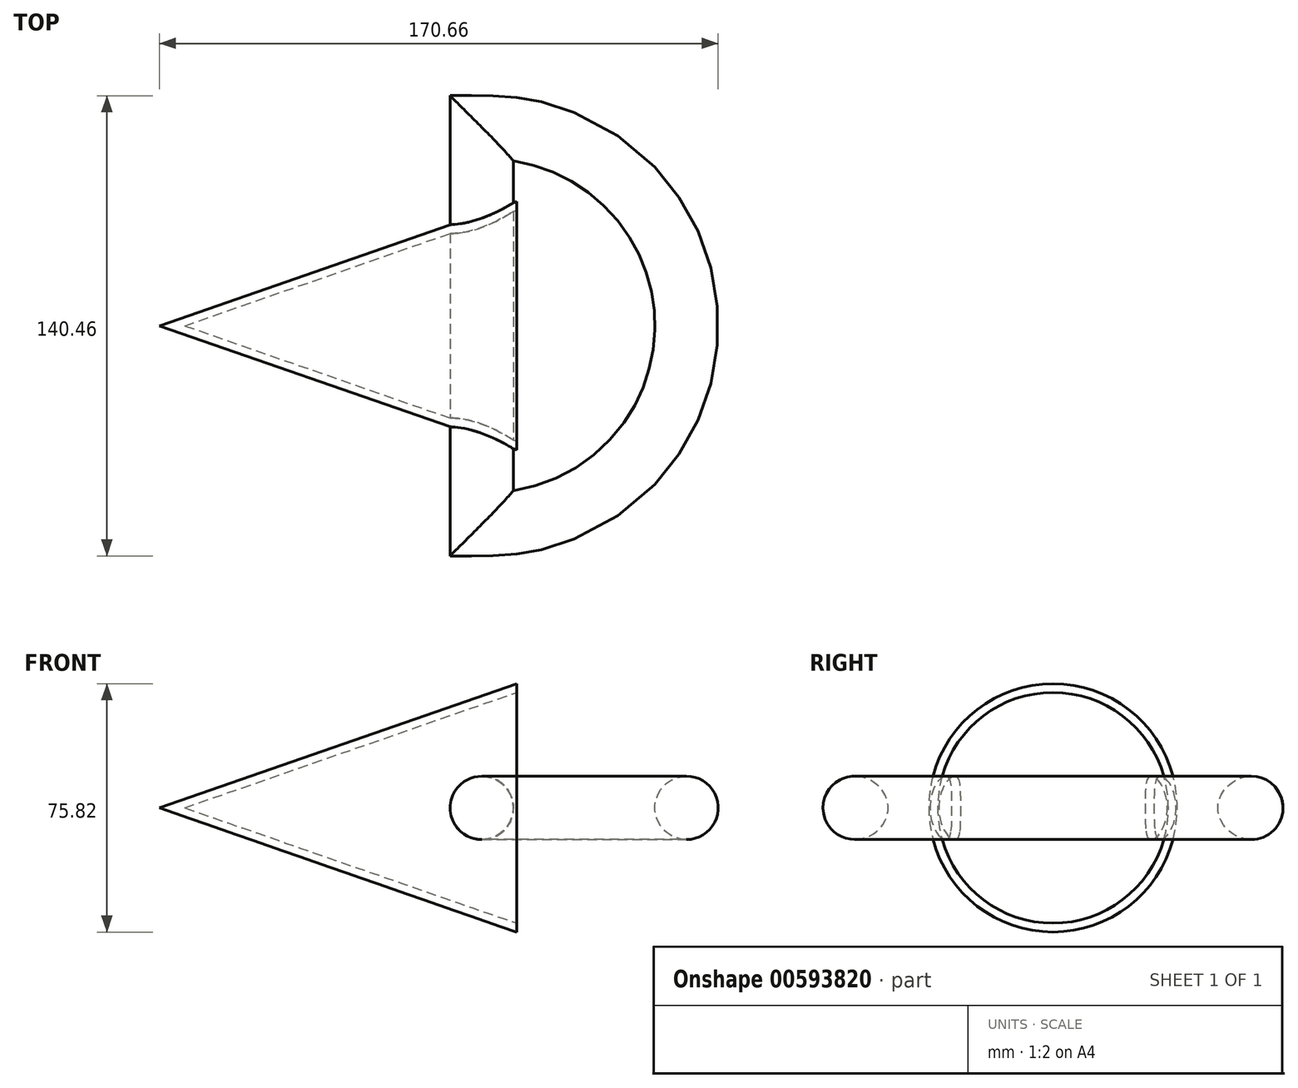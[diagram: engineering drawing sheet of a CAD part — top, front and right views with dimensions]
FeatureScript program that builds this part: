
annotation { "Feature Type Name" : "Feature", "Feature Type Description" : "" }
export const myFeature = defineFeature(function(context is Context, id is Id, definition is map)
    precondition{}
    {
        {
            var Q0;
            Q0=qCreatedBy(makeId("Front.planeOp"),FACE);
            var sketch = newSketch(context, id + "F0", { "sketchPlane" : qUnion([Q0])});
            skLineSegment(sketch, "E0", {"start": v(-65.88, 0) * mm, "end": v(43.22, 37.9) * mm});
            skLineSegment(sketch, "E1", {"start": v(43.22, 37.9) * mm, "end": v(43.22, 0) * mm});
            skLineSegment(sketch, "E2", {"start": v(43.22, 0) * mm, "end": v(-65.88, 0) * mm});
            skSolve(sketch);
        }
        {
            var Q0;
            Q0 = qSketchRegion(id + "F0", true);
            var Q1;
            Q1=sQuery(id+"F0.wireOp",EDGE,"E2");
            revolve(context, id + "F1", {"surfaceOperationType" : NewSurfaceOperationType.NEW, "entities" : qUnion([Q0]), "axis" : qUnion([Q1]), "revolveType" : RevolveType.FULL});
        }
        {
            var Q0;
            Q0=makeQuery(id+"F1.opRevolve","SWEPT_FACE",FACE,{"disambiguationData":[OSD([sQuery(id+"F0.wireOp",EDGE,"E1")])]});
            shell(context, id + "F2", {"entities" : qUnion([Q0]), "thickness" : 2.54 * mm});
        }
        {
            var Q0;
            Q0=qCreatedBy(makeId("Front.planeOp"),FACE);
            var sketch = newSketch(context, id + "F3", { "sketchPlane" : qUnion([Q0])});
            skLineSegment(sketch, "E3", {"start": v(32.6, 0) * mm, "end": v(49.66, 0) * mm});
            skCircle(sketch, "E4", {"center": v(32.6, 0) * mm, "radius": 9.67 * mm});
            skSolve(sketch);
        }
        {
            var Q0;
            Q0=qCreatedBy(makeId("Top.planeOp"),FACE);
            var sketch = newSketch(context, id + "F4", { "sketchPlane" : qUnion([Q0])});
            skLineSegment(sketch, "E5", {"start": v(34.55, 0) * mm, "end": v(34.55, 58.6) * mm});
            skArc(sketch, "E6", {"start": v(34.55, 58.6) * mm, "mid": v(93.16, 0) * mm, "end": v(34.55, -58.6) * mm});
            skLineSegment(sketch, "E7", {"start": v(34.55, -58.6) * mm, "end": v(34.55, 0) * mm});
            skSolve(sketch);
        }
        {
            var Q0;
            Q0=makeQuery(id+"F3.imprint","IMPRINT",FACE,{"disambiguationData":[TD([[makeQuery(id+"F3.imprint","IMPRINT",EDGE,{"derivedFrom":sQuery(id+"F3.wireOp",EDGE,"E4")}),1.0]])]});
            var Q1;
            Q1=sQuery(id+"F4.wireOp",EDGE,"E5");
            var Q2;
            Q2=sQuery(id+"F4.wireOp",EDGE,"E6");
            var Q3;
            Q3=sQuery(id+"F4.wireOp",EDGE,"E7");
            sweep(context, id + "F5", {"operationType" : NewBodyOperationType.ADD, "profiles" : qUnion([Q0]), "path" : qUnion([Q1, Q2, Q3])});
        }
    });
